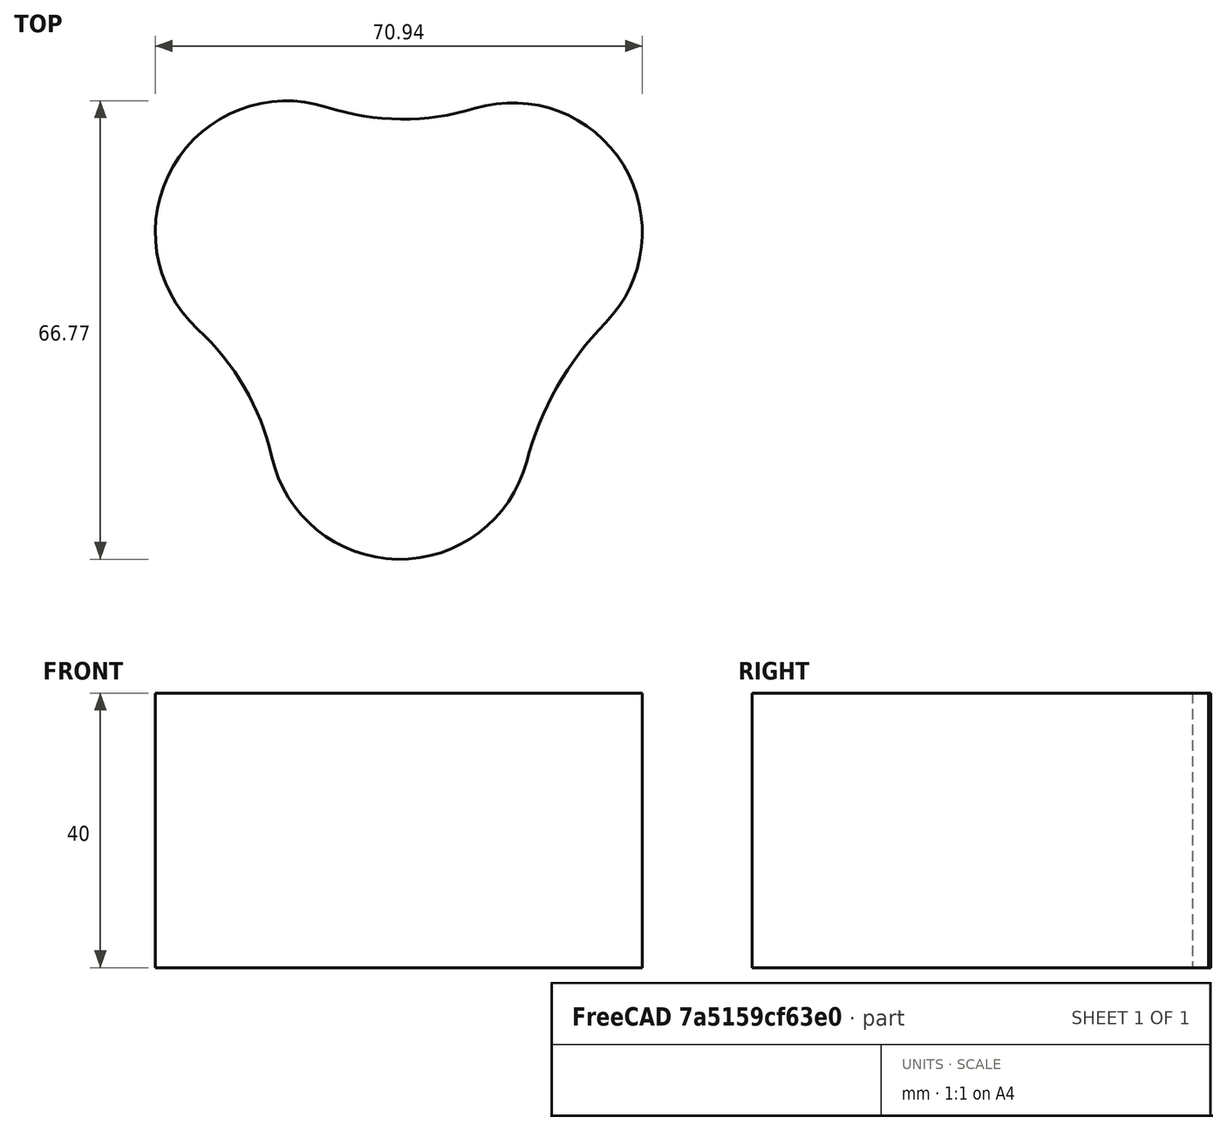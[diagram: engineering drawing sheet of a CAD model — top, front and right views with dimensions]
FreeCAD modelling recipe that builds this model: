
FCSTD DOCUMENT  (FreeCAD 1.1R20260325 (Git shallow))
Label: Stethiscope002
License: All rights reserved
LicenseURL: https://en.wikipedia.org/wiki/All_rights_reserved
objects: Sketcher::SketchObject×2, App::Point×1, PartDesign::Pad×1, PartDesign::Body×1
note: 8 computed .brp shape members not serialized (recipe doc carries the construction recipe); baked Part::Feature solids carry a one-line shape summary decoded from their .brp

FEATURE [App::Point] Origin001
  Role = Origin
FEATURE [Sketcher::SketchObject] Sketch
  ArcFitTolerance = 1e-06
  AttachmentSupport = -> [Origin]
  ExternalTypes = [0]
  FullyConstrained = false
  MakeInternals = false
  MapMode = 5
  _ExternalGeoVersion = 1
  sketch-geometry (16):
    g0: Circle [constr] CenterX=69.6034 CenterY=60.8707 CenterZ=0 NormalX=0 NormalY=0 NormalZ=1 AngleXU=0 Radius=38
    g1: LineSegment [constr] StartX=31.6034 StartY=60.8707 StartZ=0 EndX=107.603 EndY=60.8707 EndZ=0
    g2: LineSegment [constr] StartX=69.6034 StartY=60.8707 StartZ=0 EndX=102.512 EndY=79.8707 EndZ=0
    g3: LineSegment [constr] StartX=69.6034 StartY=60.8707 StartZ=0 EndX=36.6944 EndY=79.8707 EndZ=0
    g4: LineSegment [constr] StartX=69.6034 StartY=60.8707 StartZ=0 EndX=69.6034 EndY=22.8707 EndZ=0
    g5: ArcOfCircle CenterX=86.0579 CenterY=70.3707 CenterZ=0 NormalX=0 NormalY=0 NormalZ=1 AngleXU=0 Radius=18.8772 StartAngle=5.51 EndAngle=8.14961
    g6: ArcOfCircle CenterX=69.6034 CenterY=41.8707 CenterZ=0 NormalX=0 NormalY=0 NormalZ=1 AngleXU=0 Radius=19.1225 StartAngle=3.36277 EndAngle=6.0236
    g7: ArcOfCircle CenterX=53.1489 CenterY=70.3707 CenterZ=0 NormalX=0 NormalY=0 NormalZ=1 AngleXU=0 Radius=19.1482 StartAngle=1.25945 EndAngle=3.9691
    g8: LineSegment [constr] StartX=69.6034 StartY=60.8707 StartZ=0 EndX=69.6034 EndY=98.8707 EndZ=0
    g9: ArcOfCircle CenterX=70.0568 CenterY=122.91 CenterZ=0 NormalX=0 NormalY=0 NormalZ=1 AngleXU=0 Radius=36.0445 StartAngle=4.40104 EndAngle=5.00802
    g10: LineSegment [constr] StartX=69.6034 StartY=60.8707 StartZ=0 EndX=36.6944 EndY=41.8707 EndZ=0
    g11: ArcOfCircle CenterX=15.8424 CenterY=29.7821 CenterZ=0 NormalX=0 NormalY=0 NormalZ=1 AngleXU=0 Radius=35.9808 StartAngle=0.221179 EndAngle=0.827507
    g12: LineSegment [constr] StartX=69.6034 StartY=60.8707 StartZ=0 EndX=102.652 EndY=42.1144 EndZ=0
    g13: ArcOfCircle CenterX=132.334 CenterY=25.2106 CenterZ=0 NormalX=0 NormalY=0 NormalZ=1 AngleXU=0 Radius=45.783 StartAngle=2.3684 EndAngle=2.88201
    g14: GeomPoint X=50.6034 Y=60.8707 Z=0
    g15: GeomPoint X=88.6034 Y=60.8707 Z=0
  constraints (35):
    c: Diameter(g0) = 76
    c: Horizontal(g1)
    c: PointOnObject(g0,g1)
    c: PointOnObject(g1,g0)
    c: PointOnObject(g1,g0)
    c: Coincident(g2,g0)
    c: PointOnObject(g2,g0)
    c: Coincident(g3,g0)
    c: PointOnObject(g3,g0)
    c: Angle(g2,g3) = 2.0944
    c: Angle(g1,g2) = 0.523599
    c: Coincident(g4,g0)
    c: PointOnObject(g4,g0)
    c: Vertical(g4)
    c: Symmetric(g2,g2,g5)
    c: Symmetric(g4,g4,g6)
    c: Symmetric(g3,g3,g7)
    c: Coincident(g8,g0)
    c: PointOnObject(g8,g0)
    c: Vertical(g8)
    c: Tangent(g9,g7) = 1.5708
    c: Tangent(g9,g5) = 1.5708
    c: Coincident(g10,g0)
    c: PointOnObject(g10,g0)
    c: Angle(g8,g10) = 2.0944
    c: Tangent(g11,g6) = 1.5708
    c: Tangent(g11,g7) = 1.5708
    c: Coincident(g12,g0)
    c: PointOnObject(g12,g0)
    c: Tangent(g13,g5) = 1.5708
    c: Tangent(g13,g6) = 1.5708
    c: PointOnObject(g14,g1)
    c: PointOnObject(g15,g1)
    c: DistanceX(g1,g14) = 19
    c: DistanceX(g15,g1) = 19
FEATURE [PartDesign::Pad] Pad
  Direction = (0,0,1)
  Length = 40
  Length2 = 10
  Profile = -> Sketch
  ReferenceAxis = -> Sketch [N_Axis]
  Refine = true
  SideType = 0
  Suppressed = false
  Type = 0
  Type2 = 0
FEATURE [Sketcher::SketchObject] Sketch001
  ArcFitTolerance = 1e-06
  AttachmentOffset = pos=(0,0,-61) rot=(0,0,1;0rad)
  AttachmentSupport = -> [Origin]
  ExternalGeometry = -> [Sketch]
  ExternalTypes = [0,0]
  FullyConstrained = false
  MakeInternals = false
  MapMode = 5
  Placement = pos=(0,61,-1.35e-14) rot=(1,0,0;1.5708rad)
  _ExternalGeoVersion = 1
  sketch-geometry (9):
    g0: LineSegment [constr] StartX=50.6034 StartY=1.35e-14 StartZ=0 EndX=88.6034 EndY=1.35e-14 EndZ=0
    g1: LineSegment [constr] StartX=69.6034 StartY=1.35e-14 StartZ=0 EndX=69.6034 EndY=55.821 EndZ=0
    g2: LineSegment StartX=69.6034 StartY=46.3647 StartZ=0 EndX=120.942 EndY=46.3647 EndZ=0
    g3: LineSegment StartX=120.942 StartY=46.3647 StartZ=0 EndX=120.942 EndY=43.787 EndZ=0
    g4: LineSegment StartX=120.942 StartY=43.787 StartZ=0 EndX=120.815 EndY=42.6392 EndZ=0
    g5: LineSegment StartX=120.815 StartY=42.6392 StartZ=0 EndX=114.279 EndY=7.33602 EndZ=0
    g6: LineSegment StartX=114.279 StartY=7.33602 StartZ=0 EndX=114.279 EndY=2.43679 EndZ=0
    g7: LineSegment StartX=114.279 StartY=2.43679 StartZ=0 EndX=69.6034 EndY=10.7572 EndZ=0
    g8: LineSegment StartX=69.6034 StartY=46.3647 StartZ=0 EndX=69.6034 EndY=10.7572 EndZ=0
  constraints (16):
    c: Coincident(g0,g-3)
    c: Coincident(g0,g-4)
    c: Symmetric(g0,g0,g1)
    c: Vertical(g1)
    c: PointOnObject(g2,g1)
    c: Horizontal(g2)
    c: Coincident(g2,g3)
    c: Vertical(g3)
    c: Coincident(g3,g4)
    c: Coincident(g4,g5)
    c: Coincident(g5,g6)
    c: Vertical(g6)
    c: Coincident(g6,g7)
    c: PointOnObject(g7,g1)
    c: Coincident(g8,g2)
    c: Coincident(g8,g7)
FEATURE [PartDesign::Body] Body
  AllowCompound = true
  Group = -> [Sketch,Pad,Sketch001]
  Origin = -> Origin
  Tip = -> Pad
